FCSTD DOCUMENT  (FreeCAD 1.0R39319 (Git))
Label: session2_drawing2
License: All rights reserved
LicenseURL: https://en.wikipedia.org/wiki/All_rights_reserved
objects: Sketcher::SketchObject×1, PartDesign::Body×1
note: 3 computed .brp shape members not serialized (recipe doc carries the construction recipe); baked Part::Feature solids carry a one-line shape summary decoded from their .brp

FEATURE [Sketcher::SketchObject] Sketch
  ArcFitTolerance = 1e-06
  AttachmentSupport = -> [XY_Plane]
  FullyConstrained = false
  MakeInternals = false
  MapMode = 5
  sketch-geometry (27):
    g0: ArcOfCircle CenterX=-49 CenterY=0 CenterZ=0 NormalX=0 NormalY=0 NormalZ=1 AngleXU=0 Radius=19.1913 StartAngle=1.71212 EndAngle=4.71239
    g1: ArcOfCircle CenterX=-57.9009 CenterY=62.5613 CenterZ=0 NormalX=0 NormalY=0 NormalZ=1 AngleXU=0 Radius=44 StartAngle=4.85372 EndAngle=6.89965
    g2: ArcOfCircle CenterX=-49 CenterY=-35.1913 CenterZ=0 NormalX=0 NormalY=0 NormalZ=1 AngleXU=0 Radius=16 StartAngle=0.898561 EndAngle=1.5708
    g3: ArcOfCircle CenterX=-17.2404 CenterY=4.71267 CenterZ=0 NormalX=0 NormalY=0 NormalZ=1 AngleXU=0 Radius=35 StartAngle=4.04015 EndAngle=4.50091
    g4: ArcOfCircle CenterX=0 CenterY=-58.3557 CenterZ=0 NormalX=0 NormalY=0 NormalZ=1 AngleXU=0 Radius=14.9085 StartAngle=2.70018 EndAngle=4.71239
    g5: ArcOfCircle CenterX=61.476 CenterY=-51.2642 CenterZ=0 NormalX=0 NormalY=0 NormalZ=1 AngleXU=0 Radius=22 StartAngle=4.71239 EndAngle=6.37367
    g6: GeomPoint [constr] X=69.2143 Y=-60.7892 Z=0
    g7: ArcOfCircle CenterX=48 CenterY=19 CenterZ=0 NormalX=0 NormalY=0 NormalZ=1 AngleXU=0 Radius=11 StartAngle=6.17414 EndAngle=9.31573
    g8: ArcOfCircle CenterX=40.6199 CenterY=-48.409 CenterZ=0 NormalX=0 NormalY=0 NormalZ=1 AngleXU=0 Radius=11 StartAngle=3.03255 EndAngle=6.17414
    g9: LineSegment StartX=58.9347 StartY=17.8029 StartZ=0 EndX=51.5546 EndY=-49.6061 EndZ=0
    g10: LineSegment StartX=37.0653 StartY=20.1971 StartZ=0 EndX=29.6853 EndY=-47.2118 EndZ=0
    g11: LineSegment StartX=-22 StartY=88 StartZ=0 EndX=-11 EndY=88 EndZ=0
    g12: ArcOfCircle CenterX=44.5495 CenterY=71.8568 CenterZ=0 NormalX=0 NormalY=0 NormalZ=1 AngleXU=0 Radius=27.7323 StartAngle=2.52028 EndAngle=4.91839
    g13: LineSegment [constr] StartX=0 StartY=0 StartZ=0 EndX=40.6199 EndY=-48.409 EndZ=0
    g14: LineSegment [constr] StartX=0 StartY=0 StartZ=0 EndX=0 EndY=-58.3557 EndZ=0
    g15: Circle CenterX=0 CenterY=0 CenterZ=0 NormalX=0 NormalY=0 NormalZ=1 AngleXU=0 Radius=14
    g16: Circle CenterX=0 CenterY=88 CenterZ=0 NormalX=0 NormalY=0 NormalZ=1 AngleXU=0 Radius=7
    g17: ArcOfCircle CenterX=0 CenterY=88 CenterZ=0 NormalX=0 NormalY=0 NormalZ=1 AngleXU=0 Radius=11 StartAngle=-5.69446e-10 EndAngle=3.14159
    g18: LineSegment StartX=11 StartY=88 StartZ=0 EndX=22 EndY=88 EndZ=0
    g19: ArcOfCircle CenterX=-27.9459 CenterY=-45.1511 CenterZ=0 NormalX=0 NormalY=0 NormalZ=1 AngleXU=0 Radius=16 StartAngle=5.84177 EndAngle=7.6425
    g20: Circle CenterX=-49 CenterY=0 CenterZ=0 NormalX=0 NormalY=0 NormalZ=1 AngleXU=0 Radius=8.64156
    g21: Circle CenterX=0 CenterY=-58.3557 CenterZ=0 NormalX=0 NormalY=0 NormalZ=1 AngleXU=0 Radius=10.089
    g22: LineSegment StartX=0 StartY=-73.2642 StartZ=0 EndX=61.476 EndY=-73.2642 EndZ=0
    g23: LineSegment [constr] StartX=40.6199 StartY=-48.409 StartZ=0 EndX=63.3136 EndY=-75.4542 EndZ=0
    g24: LineSegment [constr] StartX=0 StartY=-58.3557 StartZ=0 EndX=40.6199 EndY=-48.409 EndZ=0
    g25: LineSegment StartX=76.6321 StartY=25.1639 StartZ=0 EndX=83.386 EndY=-49.2764 EndZ=0
    g26: ArcOfCircle CenterX=54.7221 CenterY=23.176 CenterZ=0 NormalX=0 NormalY=0 NormalZ=1 AngleXU=0 Radius=22 StartAngle=0.0838158 EndAngle=1.7768
  constraints (61):
    c: PointOnObject(g0,g-1)
    c: Tangent(g2,g3) = 1.5708
    c: Radius(g2) = 16
    c: Radius(g3) = 35
    c: Distance(g1,g4) = 148
    c: DistanceY(g1,g1) = 69
    c: Radius(g1) = 44
    c: Tangent(g0,g1) = 1.5708
    c: Radius(g5) = 22
    c: Tangent(g7,g9) = 1.5708
    c: Tangent(g7,g10) = -1.5708
    c: Tangent(g8,g9) = 1.5708
    c: Tangent(g8,g10) = -1.5708
    c: Equal(g7,g8)
    c: Coincident(g11,g1)
    c: Horizontal(g11)
    c: Coincident(g12,g18)
    c: Radius(g7) = 11
    c: Coincident(g13,g-1)
    c: Coincident(g13,g8)
    c: Coincident(g14,g13)
    c: Coincident(g14,g4)
    c: PointOnObject(g4,g-2)
    c: Angle(g14,g13) = 0.698132
    c: Diameter(g15) = 28
    c: Distance(g15,g11) = 88
    c: DistanceX(g15,g7) = 48
    c: Coincident(g15,g13)
    c: Distance(g7,g-1) = 19
    c: Symmetric(g11,g18,g16)
    c: Coincident(g17,g16)
    c: Coincident(g11,g17)
    c: Coincident(g18,g17)
    c: Diameter(g16) = 14
    c: Radius(g17) = 11
    c: Radius(g19) = 16
    c: Coincident(g20,g0)
    c: Coincident(g21,g4)
    c: DistanceX(g16,g12) = 22
    c: Vertical(g0,g0)
    c: PointOnObject(g16,g-2)
    c: Horizontal(g18)
    c: Block(g17)
    c: Block(g16)
    c: Distance(g0,g-2) = 49
    c: PointOnObject(g4,g-2)
    c: Coincident(g23,g8)
    c: Parallel(g13,g23)
    c: PointOnObject(g5,g23)
    c: Coincident(g24,g4)
    c: Coincident(g24,g8)
    c: Tangent(g25,g5) = 1.5708
    c: Tangent(g19,g3) = 1.5708
    c: Tangent(g0,g2) = 1.5708
    c: Tangent(g4,g19) = 1.5708
    c: Tangent(g4,g22) = -1.5708
    c: Tangent(g22,g5) = -1.5708
    c: Tangent(g25,g26) = 1.5708
    c: Tangent(g25,g12)
    c: Radius(g26) = 22
    c: Tangent(g26,g12) = 1.5708
FEATURE [PartDesign::Body] Body
  AllowCompound = false
  Group = -> [Sketch]
  Origin = -> Origin
